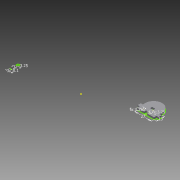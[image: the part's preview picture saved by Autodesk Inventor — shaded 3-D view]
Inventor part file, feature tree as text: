
AUTODESK INVENTOR PART (.ipt)
format: ipt  version: 2013 (Build 170138000, 138)  size: 119,808 bytes
history: native  units: mm
features: extrude x5, other x2, sketch x1
ambient origin geometry x8: Origin, YZ Plane, XZ Plane, XY Plane, X Axis, Y Axis, Z Axis, Center Point
feature tree (8):
  other  "Blocks"
  sketch  "Sketch1"  dims[d0=3.0mm d2=3.0mm d3=0.1mm d7=22.5mm d8=12.4mm d9=4.5mm d10=4.5mm d11=2.0mm d12=2.0mm d58=27.0mm d59=13.0mm d60=3.25mm d61=5.0mm d62=3.25mm d63=0.0mm d68=5.0mm d69=3.25mm d70=3.25mm d71=0.0mm d72=3.25mm d73=0.0mm d74=3.25mm d75=0.0mm d76=3.25mm d77=0.0mm]
  extrude  "Extrusion5"  Depth=3.0mm
  extrude  "Extrusion7"  Depth=27.0mm
  extrude  "Extrusion8"  Depth=13.0mm
  extrude  "Extrusion9"  Depth=3.25mm
  extrude  "Extrusion10"  Depth=5.0mm
  other  "Block1"
